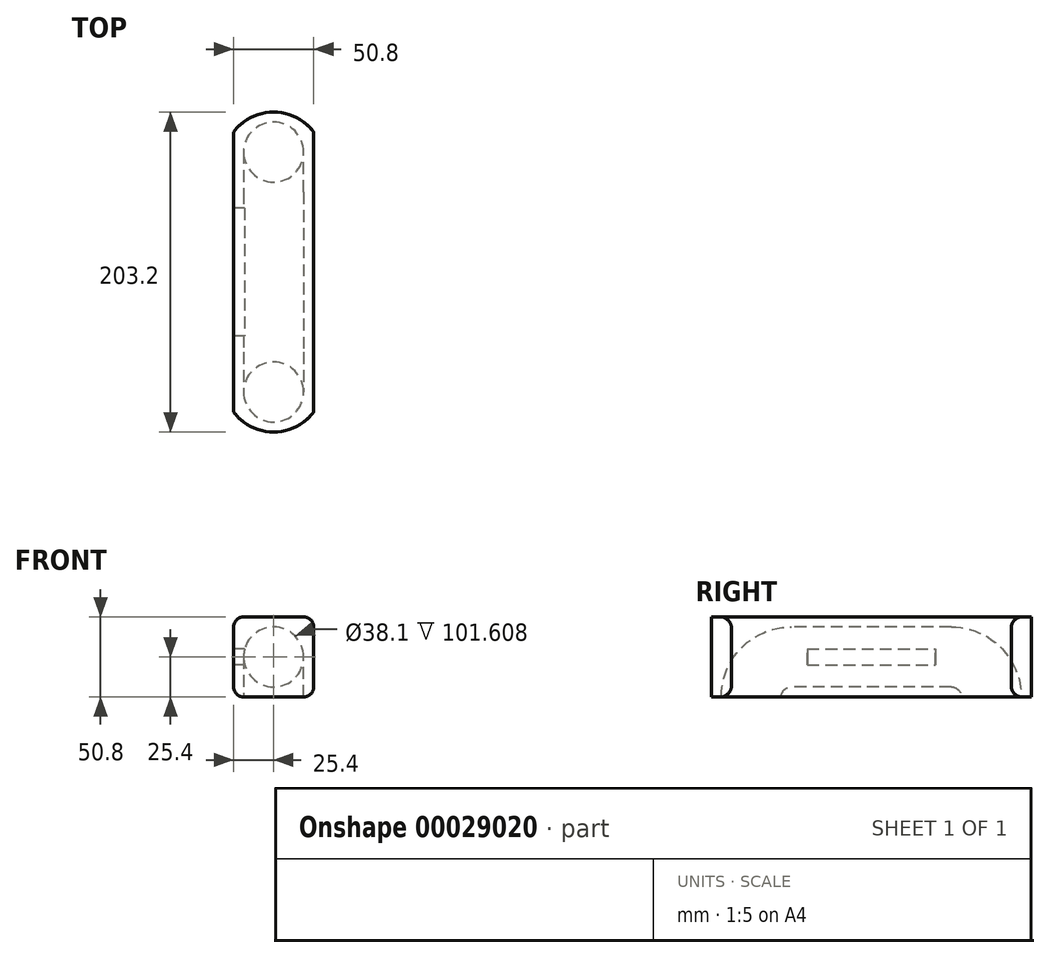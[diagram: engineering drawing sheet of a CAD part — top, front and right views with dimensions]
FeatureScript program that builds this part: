
annotation { "Feature Type Name" : "Feature", "Feature Type Description" : "" }
export const myFeature = defineFeature(function(context is Context, id is Id, definition is map)
    precondition{}
    {
        {
            var Q0;
            Q0=qCreatedBy(makeId("Front.planeOp"),FACE);
            var sketch = newSketch(context, id + "F0", { "sketchPlane" : qUnion([Q0])});
            skLineSegment(sketch, "E0.rect.bottom", {"start": v(25.4, -25.4) * mm, "end": v(-25.4, -25.4) * mm});
            skLineSegment(sketch, "E0.rect.top", {"start": v(25.4, 25.4) * mm, "end": v(-25.4, 25.4) * mm});
            skLineSegment(sketch, "E0.rect.left", {"start": v(25.4, -25.4) * mm, "end": v(25.4, 25.4) * mm});
            skLineSegment(sketch, "E0.rect.right", {"start": v(-25.4, -25.4) * mm, "end": v(-25.4, 25.4) * mm});
            skPoint(sketch, "E0.rect.middle", {"position": v(0, 0) * mm});
            skSolve(sketch);
        }
        {
            var Q0;
            Q0 = qSketchRegion(id + "F0", true);
            extrude(context, id + "F1", {"entities" : qUnion([Q0]), "depth" : 203.2 * mm});
        }
        {
            var Q0;
            Q0=makeQuery(id+"F1.opExtrude","SWEPT_FACE",FACE,{"disambiguationData":[OSD([sQuery(id+"F0.wireOp",EDGE,"E0.rect.bottom")])]});
            var sketch = newSketch(context, id + "F2", { "sketchPlane" : qUnion([Q0])});
            skLineSegment(sketch, "E1.0.0", {"start": v(-25.4, 0) * mm, "end": v(25.4, 0) * mm});
            skLineSegment(sketch, "E1.0.1", {"start": v(25.4, 0) * mm, "end": v(25.4, 203.2) * mm});
            skLineSegment(sketch, "E1.0.2", {"start": v(25.4, 203.2) * mm, "end": v(-25.4, 203.2) * mm});
            skLineSegment(sketch, "E1.0.3", {"start": v(-25.4, 203.2) * mm, "end": v(-25.4, 0) * mm});
            skCircle(sketch, "E2", {"center": v(0, 25.4) * mm, "radius": 19.05 * mm});
            skSolve(sketch);
        }
        {
            var Q0;
            Q0=makeQuery(id+"F1.opExtrude","SWEPT_FACE",FACE,{"disambiguationData":[OSD([sQuery(id+"F0.wireOp",EDGE,"E0.rect.right")])]});
            cPlane(context, id + "F3", {"entities" : qUnion([Q0]), "cplaneType" : CPlaneType.OFFSET, "offset" : 25.4 * mm, "oppositeDirection" : true, "width" : 152.4 * mm, "height" : 152.4 * mm});
        }
        {
            var Q0;
            Q0=qCreatedBy(id+"F3.planeOp",FACE);
            var sketch = newSketch(context, id + "F4", { "sketchPlane" : qUnion([Q0])});
            skLineSegment(sketch, "E3.0", {"start": v(44.44, -25.4) * mm, "end": v(6.34, -25.4) * mm});
            skLineSegment(sketch, "E4.0", {"start": v(203.2, -25.4) * mm, "end": v(203.2, 25.4) * mm});
            skLineSegment(sketch, "E5.0", {"start": v(0, -25.4) * mm, "end": v(203.2, -25.4) * mm});
            skLineSegment(sketch, "E6.0", {"start": v(0, -25.4) * mm, "end": v(0, 25.4) * mm});
            skLineSegment(sketch, "E7", {"start": v(50.8, 0) * mm, "end": v(152.4, 0) * mm});
            skLineSegment(sketch, "E8", {"start": v(25.4, -25.4) * mm, "end": v(25.4, -25.4) * mm});
            skLineSegment(sketch, "E9", {"start": v(177.8, -25.4) * mm, "end": v(177.8, -25.4) * mm});
            skPoint(sketch, "E10.newPointA", {"position": v(25.4, 0) * mm});
            skArc(sketch, "E10.filletArc", {"start": v(50.8, 0) * mm, "mid": v(32.83, -7.44) * mm, "end": v(25.4, -25.4) * mm});
            skPoint(sketch, "E11.newPointA", {"position": v(177.8, 0) * mm});
            skPoint(sketch, "E11.newPointB", {"position": v(203.2, 0) * mm});
            skArc(sketch, "E11.filletArc", {"start": v(177.8, -25.4) * mm, "mid": v(170.36, -7.44) * mm, "end": v(152.4, 0) * mm});
            skSolve(sketch);
        }
        {
            var Q0;
            Q0=makeQuery(id+"F2.imprint","IMPRINT",FACE,{"disambiguationData":[TD([[makeQuery(id+"F2.imprint","IMPRINT",EDGE,{"derivedFrom":sQuery(id+"F2.wireOp",EDGE,"E2")}),1.0]])]});
            var Q1;
            Q1=sQuery(id+"F4.wireOp",EDGE,"E10.filletArc");
            var Q2;
            Q2=sQuery(id+"F4.wireOp",EDGE,"E7");
            var Q3;
            Q3=sQuery(id+"F4.wireOp",EDGE,"E11.filletArc");
            sweep(context, id + "F5", {"operationType" : NewBodyOperationType.REMOVE, "profiles" : qUnion([Q0]), "path" : qUnion([Q1, Q2, Q3])});
        }
        {
            var Q0;
            Q0=makeQuery(id+"F1.opExtrude","SWEPT_FACE",FACE,{"disambiguationData":[OSD([sQuery(id+"F0.wireOp",EDGE,"E0.rect.right")])]});
            var sketch = newSketch(context, id + "F6", { "sketchPlane" : qUnion([Q0])});
            skLineSegment(sketch, "E12.rect.bottom", {"start": v(142.2, -5.08) * mm, "end": v(61, -5.08) * mm});
            skLineSegment(sketch, "E12.rect.top", {"start": v(142.2, 5.08) * mm, "end": v(61, 5.08) * mm});
            skLineSegment(sketch, "E12.rect.left", {"start": v(142.2, -5.08) * mm, "end": v(142.2, 5.08) * mm});
            skLineSegment(sketch, "E12.rect.right", {"start": v(61, -5.08) * mm, "end": v(61, 5.08) * mm});
            skSolve(sketch);
        }
        {
            var Q0;
            Q0=makeQuery(id+"F6.imprint","IMPRINT",FACE,{"disambiguationData":[TD([[makeQuery(id+"F6.imprint","IMPRINT",EDGE,{"derivedFrom":sQuery(id+"F6.wireOp",EDGE,"E12.rect.bottom")}),-1.0]])]});
            extrude(context, id + "F7", {"entities" : qUnion([Q0]), "operationType" : NewBodyOperationType.REMOVE, "oppositeDirection" : true, "depth" : 25.4 * mm});
        }
        {
            var Q0;
            {var subQ0=sQuery(id+"F0.wireOp",EDGE,"E0.rect.bottom");Q0=makeQuery(id+"FL3a3cW26J48OLM_1.boolean.opBoolean","MERGE",FACE,{"derivedFrom":[makeQuery(id+"Fl0AAqNo5yzz4Ik_1.boolean.opBoolean","MERGE",FACE,{"derivedFrom":[makeQuery(id+"F1.opExtrude","SWEPT_FACE",FACE,{"disambiguationData":[OSD([subQ0])]}),makeQuery(id+"Fl0AAqNo5yzz4Ik_1.opExtrude","SWEPT_FACE",FACE,{"disambiguationData":[OSD([subQ0])]})]}),makeQuery(id+"FL3a3cW26J48OLM_1.opExtrude","SWEPT_FACE",FACE,{"disambiguationData":[OSD([subQ0])]})]});}
            var sketch = newSketch(context, id + "F8", { "sketchPlane" : qUnion([Q0])});
            skLineSegment(sketch, "E13", {"start": v(25.4, 0) * mm, "end": v(-25.4, 0) * mm});
            skCircle(sketch, "E14", {"center": v(0, 31.75) * mm, "radius": 31.75 * mm});
            skPoint(sketch, "E14.centerSnap0", {"position": v(0, 0) * mm});
            skCircle(sketch, "E15", {"center": v(0, 171.45) * mm, "radius": 31.75 * mm});
            skSolve(sketch);
        }
        {
            var Q0;
            {var subQ1=sQuery(id+"F8.wireOp",EDGE,"E14");var subQ3=sQuery(id+"F8.wireOp",EDGE,"E13");var subQ5=makeQuery(id+"F8.imprint","INTERSECT",VERTEX,{"derivedFrom":[subQ3,subQ1]});Q0=makeQuery(id+"F8.imprint","IMPRINT",FACE,{"disambiguationData":[TD([[makeQuery(id+"F8.imprint","IMPRINT",EDGE,{"disambiguationData":[TD([[subQ5,-1.0]])],"derivedFrom":subQ3}),-1.0]])]});}
            var Q1;
            {var subQ1=sQuery(id+"F8.wireOp",EDGE,"E14");var subQ3=sQuery(id+"F8.wireOp",EDGE,"E13");var subQ5=makeQuery(id+"F8.imprint","INTERSECT",VERTEX,{"derivedFrom":[subQ3,subQ1]});Q1=makeQuery(id+"F8.imprint","IMPRINT",FACE,{"disambiguationData":[TD([[makeQuery(id+"F8.imprint","IMPRINT",EDGE,{"disambiguationData":[TD([[subQ5,1.0]])],"derivedFrom":subQ3}),-1.0]])]});}
            extrude(context, id + "F9", {"entities" : qUnion([Q0, Q1]), "operationType" : NewBodyOperationType.REMOVE, "endBound" : BoundingType.THROUGH_ALL, "oppositeDirection" : true, "depth" : 25.4 * mm});
        }
        {
            var Q0;
            Q0=makeQuery(id+"F1.opExtrude","SWEPT_EDGE",EDGE,{"disambiguationData":[OSD([sQuery(id+"F0.wireOp",EDGE,"E0.rect.bottom"),sQuery(id+"F0.wireOp",EDGE,"E0.rect.right")])]});
            var Q1;
            Q1=makeQuery(id+"F1.opExtrude","SWEPT_EDGE",EDGE,{"disambiguationData":[OSD([sQuery(id+"F0.wireOp",EDGE,"E0.rect.top"),sQuery(id+"F0.wireOp",EDGE,"E0.rect.right")])]});
            var Q2;
            Q2=makeQuery(id+"F1.opExtrude","SWEPT_EDGE",EDGE,{"disambiguationData":[OSD([sQuery(id+"F0.wireOp",EDGE,"E0.rect.bottom"),sQuery(id+"F0.wireOp",EDGE,"E0.rect.left")])]});
            var Q3;
            Q3=makeQuery(id+"F1.opExtrude","SWEPT_EDGE",EDGE,{"disambiguationData":[OSD([sQuery(id+"F0.wireOp",EDGE,"E0.rect.top"),sQuery(id+"F0.wireOp",EDGE,"E0.rect.left")])]});
            fillet(context, id + "F10", {"entities" : qUnion([Q0, Q1, Q2, Q3]), "radius" : 6.35 * mm, "tangentPropagation" : true, "allowEdgeOverflow" : false});
        }
        {
            var Q0;
            {var subQ0=sQuery(id+"F0.wireOp",EDGE,"E0.rect.bottom");var subQ1=makeQuery(id+"F1.opExtrude","CAP_EDGE",EDGE,{"disambiguationData":[OSD([subQ0])],"isStart":false});var subQ2=sQuery(id+"F8.wireOp",EDGE,"E15");var subQ3=makeQuery(id+"F8.imprint","INTERSECT",VERTEX,{"derivedFrom":[subQ1,subQ2]});Q0=makeQuery(id+"F8.imprint","IMPRINT",FACE,{"disambiguationData":[TD([[makeQuery(id+"F8.imprint","IMPRINT",EDGE,{"disambiguationData":[TD([[subQ3,-1.0]])],"derivedFrom":subQ2}),-1.0]])]});}
            var Q1;
            {var subQ0=sQuery(id+"F0.wireOp",EDGE,"E0.rect.bottom");var subQ1=makeQuery(id+"F1.opExtrude","CAP_EDGE",EDGE,{"disambiguationData":[OSD([subQ0])],"isStart":false});var subQ2=sQuery(id+"F8.wireOp",EDGE,"E15");var subQ3=makeQuery(id+"F8.imprint","INTERSECT",VERTEX,{"derivedFrom":[subQ1,subQ2]});Q1=makeQuery(id+"F8.imprint","IMPRINT",FACE,{"disambiguationData":[TD([[makeQuery(id+"F8.imprint","IMPRINT",EDGE,{"disambiguationData":[TD([[subQ3,1.0]])],"derivedFrom":subQ2}),-1.0]])]});}
            extrude(context, id + "F11", {"entities" : qUnion([Q0, Q1]), "operationType" : NewBodyOperationType.REMOVE, "oppositeDirection" : true, "depth" : 50.8 * mm});
        }
    });
